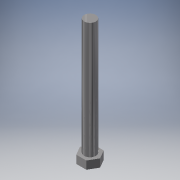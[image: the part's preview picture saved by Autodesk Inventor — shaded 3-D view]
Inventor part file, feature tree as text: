
AUTODESK INVENTOR PART (.ipt)
format: ipt  version: 2016 (Build 200138000, 138)  size: 118,784 bytes
history: native  units: in
note: dims shown in document units (in); Inventor stores cm internally (conversion verified against a paired STEP export)
features: extrude x2, sketch x2
ambient origin geometry x8: Origin, YZ Plane, XZ Plane, XY Plane, X Axis, Y Axis, Z Axis, Center Point
bodies: Solid1 (feature_tree)
feature tree (4):
  extrude  "Extrusion1"  Depth=0.3438in TaperAngle=0.0deg
  extrude  "Extrusion2"  Depth=5.0in TaperAngle=0.0deg
  sketch  "Sketch1"  dims[d0=0.75in d1=0.3438in d2=0.0in]
  sketch  "Sketch2"  dims[d3=0.5in d4=5.0in d5=0.0in]
